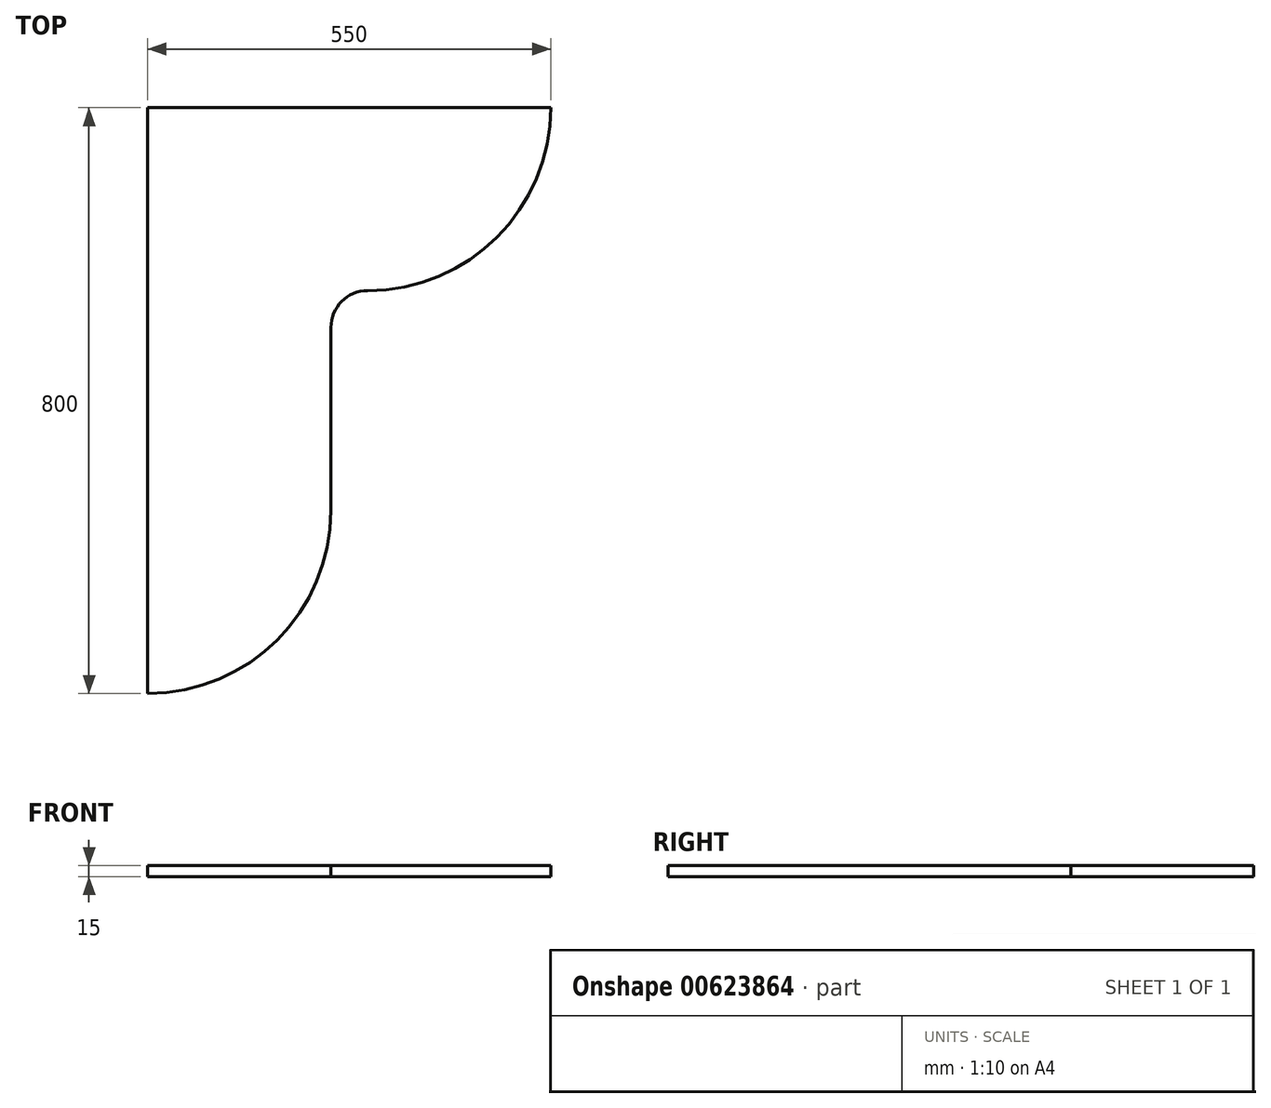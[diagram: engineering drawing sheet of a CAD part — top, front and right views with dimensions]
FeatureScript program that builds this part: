
annotation { "Feature Type Name" : "Feature", "Feature Type Description" : "" }
export const myFeature = defineFeature(function(context is Context, id is Id, definition is map)
    precondition{}
    {
        {
            var Q0;
            Q0=qCreatedBy(makeId("Top.planeOp"),FACE);
            var sketch = newSketch(context, id + "F0", { "sketchPlane" : qUnion([Q0])});
            skLineSegment(sketch, "E0", {"start": v(0, 0) * mm, "end": v(550, 0) * mm});
            skArc(sketch, "E1", {"start": v(300, -250) * mm, "mid": v(476.78, -176.78) * mm, "end": v(550, 0) * mm});
            skLineSegment(sketch, "E2", {"start": v(300, -250) * mm, "end": v(300, -250) * mm});
            skArc(sketch, "E3", {"start": v(300, -250) * mm, "mid": v(264.64, -264.64) * mm, "end": v(250, -300) * mm});
            skLineSegment(sketch, "E4", {"start": v(250, -300) * mm, "end": v(250, -550) * mm});
            skArc(sketch, "E5", {"start": v(0, -800) * mm, "mid": v(176.78, -726.78) * mm, "end": v(250, -550) * mm});
            skLineSegment(sketch, "E6", {"start": v(0, 0) * mm, "end": v(0, -800) * mm});
            skSolve(sketch);
        }
        {
            var Q0;
            Q0 = qSketchRegion(id + "F0", true);
            extrude(context, id + "F1", {"entities" : qUnion([Q0]), "depth" : 15 * mm, "offsetDistance" : 25 * mm});
        }
    });
